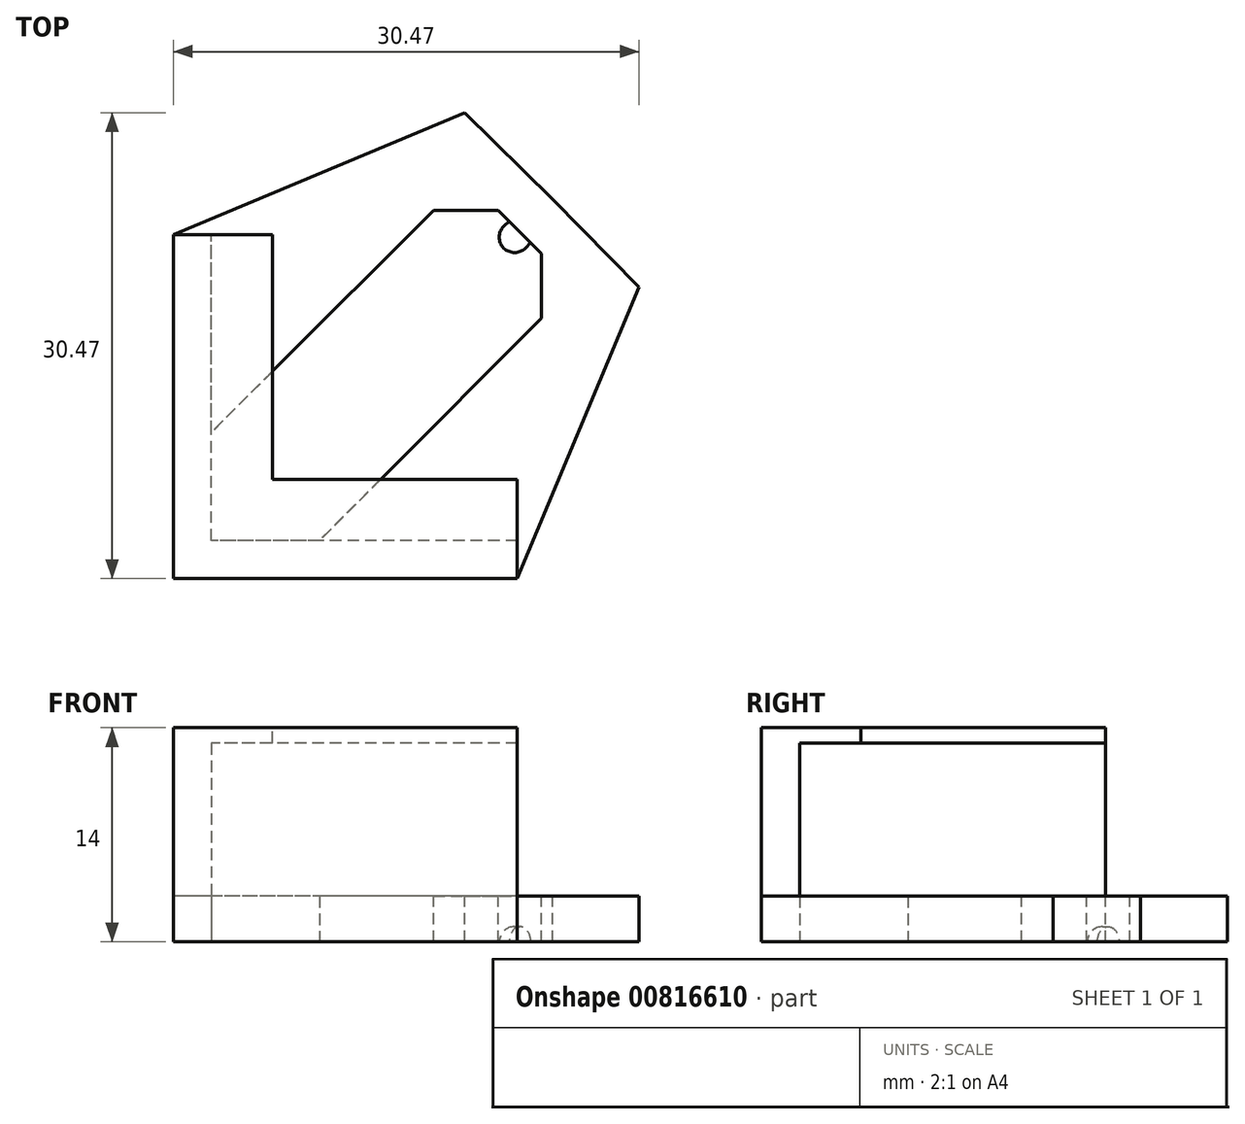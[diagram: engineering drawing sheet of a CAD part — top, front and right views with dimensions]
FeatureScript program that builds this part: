
annotation { "Feature Type Name" : "Feature", "Feature Type Description" : "" }
export const myFeature = defineFeature(function(context is Context, id is Id, definition is map)
    precondition{}
    {
        {
            var Q0;
            Q0=qCreatedBy(makeId("Top.planeOp"),FACE);
            cPlane(context, id + "F0", {"entities" : qUnion([Q0]), "cplaneType" : CPlaneType.OFFSET, "offset" : 4 * mm, "width" : 150 * mm, "height" : 150 * mm});
        }
        {
            var Q0;
            Q0=qCreatedBy(id+"F0.planeOp",FACE);
            var sketch = newSketch(context, id + "F1", { "sketchPlane" : qUnion([Q0])});
            skLineSegment(sketch, "E0", {"start": v(0, 0) * mm, "end": v(0, 20) * mm});
            skLineSegment(sketch, "E1", {"start": v(0, 20) * mm, "end": v(-2.5, 20) * mm});
            skLineSegment(sketch, "E2", {"start": v(-2.5, 20) * mm, "end": v(-2.5, -2.5) * mm});
            skLineSegment(sketch, "E3", {"start": v(-2.5, -2.5) * mm, "end": v(20, -2.5) * mm});
            skLineSegment(sketch, "E4", {"start": v(20, -2.5) * mm, "end": v(20, 0) * mm});
            skLineSegment(sketch, "E5", {"start": v(20, 0) * mm, "end": v(0, 0) * mm});
            skSolve(sketch);
        }
        {
            var Q0;
            Q0=qSketchRegion(id+"F1",true);
            extrude(context, id + "F2", {"entities" : qUnion([Q0]), "depth" : 7 * mm, "offsetDistance" : 25 * mm});
        }
        {
            var Q0;
            Q0=qCreatedBy(makeId("Top.planeOp"),FACE);
            var sketch = newSketch(context, id + "F3", { "sketchPlane" : qUnion([Q0])});
            skLineSegment(sketch, "E6", {"start": v(-2.5, 20) * mm, "end": v(20, -2.5) * mm, "construction": true});
            skLineSegment(sketch, "E7.top", {"start": v(21.6, 14.52) * mm, "end": v(4.57, -2.5) * mm});
            skLineSegment(sketch, "E7.left", {"start": v(20.18, 20.18) * mm, "end": v(21.6, 18.76) * mm});
            skPoint(sketch, "E7.middle", {"position": v(8.75, 8.75) * mm});
            skLineSegment(sketch, "E8.bottom", {"start": v(27.97, 16.56) * mm, "end": v(22.3, 22.3) * mm});
            skLineSegment(sketch, "E9", {"start": v(4.57, -2.5) * mm, "end": v(8.75, -2.5) * mm});
            skLineSegment(sketch, "E10", {"start": v(21.6, 14.52) * mm, "end": v(21.6, 18.76) * mm});
            skPoint(sketch, "E11.end.orphan", {"position": v(-2.5, 4.57) * mm});
            skLineSegment(sketch, "E12.MirrorCS", {"start": v(-2.5, 4.57) * mm, "end": v(-2.5, 8.75) * mm});
            skLineSegment(sketch, "E13.MirrorCS", {"start": v(14.52, 21.6) * mm, "end": v(-2.5, 4.57) * mm});
            skLineSegment(sketch, "E14.MirrorCS", {"start": v(20.18, 20.18) * mm, "end": v(18.76, 21.6) * mm});
            skLineSegment(sketch, "E15.MirrorCS", {"start": v(14.52, 21.6) * mm, "end": v(18.76, 21.6) * mm});
            skLineSegment(sketch, "E16.MirrorCS", {"start": v(16.56, 27.97) * mm, "end": v(22.3, 22.3) * mm});
            skLineSegment(sketch, "E17", {"start": v(27.97, 16.56) * mm, "end": v(20, -2.5) * mm});
            skLineSegment(sketch, "E18", {"start": v(8.75, -2.5) * mm, "end": v(20, -2.5) * mm});
            skLineSegment(sketch, "E19", {"start": v(16.56, 27.97) * mm, "end": v(-2.5, 20) * mm});
            skLineSegment(sketch, "E20", {"start": v(-2.5, 20) * mm, "end": v(-2.5, 8.75) * mm});
            skSolve(sketch);
        }
        {
            var Q0;
            Q0=qSketchRegion(id+"F3",true);
            extrude(context, id + "F4", {"entities" : qUnion([Q0]), "operationType" : NewBodyOperationType.ADD, "depth" : -3 * mm, "offsetDistance" : 25 * mm});
        }
        {
            var Q0;
            Q0=qSketchRegion(id+"F1",true);
            extrude(context, id + "F5", {"entities" : qUnion([Q0]), "operationType" : NewBodyOperationType.ADD, "depth" : -7 * mm, "offsetDistance" : 25 * mm});
        }
        {
            var Q0;
            Q0=makeQuery(id+"F4.opExtrude","SWEPT_FACE",FACE,{"disambiguationData":[OSD([sQuery(id+"F3.wireOp",EDGE,"E7.left"),sQuery(id+"F3.wireOp",EDGE,"E14.MirrorCS")])]});
            var sketch = newSketch(context, id + "F6", { "sketchPlane" : qUnion([Q0])});
            skArc(sketch, "E21", {"start": v(1, -3) * mm, "mid": v(0, -2) * mm, "end": v(-1, -3) * mm});
            skLineSegment(sketch, "E22", {"start": v(-1, -3) * mm, "end": v(1, -3) * mm});
            skSolve(sketch);
        }
        {
            var Q0;
            Q0=makeQuery(id+"F6.imprint","IMPRINT",FACE,{"disambiguationData":[TD([[makeQuery(id+"F6.imprint","IMPRINT",EDGE,{"derivedFrom":sQuery(id+"F6.wireOp",EDGE,"E21")}),1.0]])]});
            extrude(context, id + "F7", {"entities" : qUnion([Q0]), "operationType" : NewBodyOperationType.ADD, "depth" : 1.5 * mm, "offsetDistance" : 25 * mm});
        }
        {
            var Q0;
            Q0=makeQuery(id+"F7.opExtrude","CAP_EDGE",EDGE,{"disambiguationData":[OSD([sQuery(id+"F6.wireOp",EDGE,"E21")])],"isStart":false});
            fillet(context, id + "F8", {"entities" : qUnion([Q0]), "radius" : 1 * mm, "tangentPropagation" : true, "allowEdgeOverflow" : false});
        }
        {
            var Q0;
            Q0=makeQuery(id+"F2.opExtrude","CAP_FACE",FACE,{"disambiguationData":[OSD([sQuery(id+"F1.wireOp",EDGE,"E0"),sQuery(id+"F1.wireOp",EDGE,"E1"),sQuery(id+"F1.wireOp",EDGE,"E2"),sQuery(id+"F1.wireOp",EDGE,"E3"),sQuery(id+"F1.wireOp",EDGE,"E4"),sQuery(id+"F1.wireOp",EDGE,"E5")])],"isStart":false});
            var sketch = newSketch(context, id + "F9", { "sketchPlane" : qUnion([Q0])});
            skLineSegment(sketch, "E23.0", {"start": v(-2.5, 20) * mm, "end": v(-2.5, -2.5) * mm});
            skLineSegment(sketch, "E23.2", {"start": v(20, 4) * mm, "end": v(4, 4) * mm});
            skLineSegment(sketch, "E23.3", {"start": v(-2.5, -2.5) * mm, "end": v(20, -2.5) * mm});
            skLineSegment(sketch, "E23.4", {"start": v(4, 4) * mm, "end": v(4, 20) * mm});
            skLineSegment(sketch, "E24", {"start": v(-2.5, 20) * mm, "end": v(4, 20) * mm});
            skLineSegment(sketch, "E25", {"start": v(20, -2.5) * mm, "end": v(20, 4) * mm});
            skSolve(sketch);
        }
        {
            var Q0;
            Q0=qSketchRegion(id+"F9",true);
            extrude(context, id + "F10", {"entities" : qUnion([Q0]), "operationType" : NewBodyOperationType.ADD, "depth" : -1 * mm, "offsetDistance" : 25 * mm});
        }
    });
